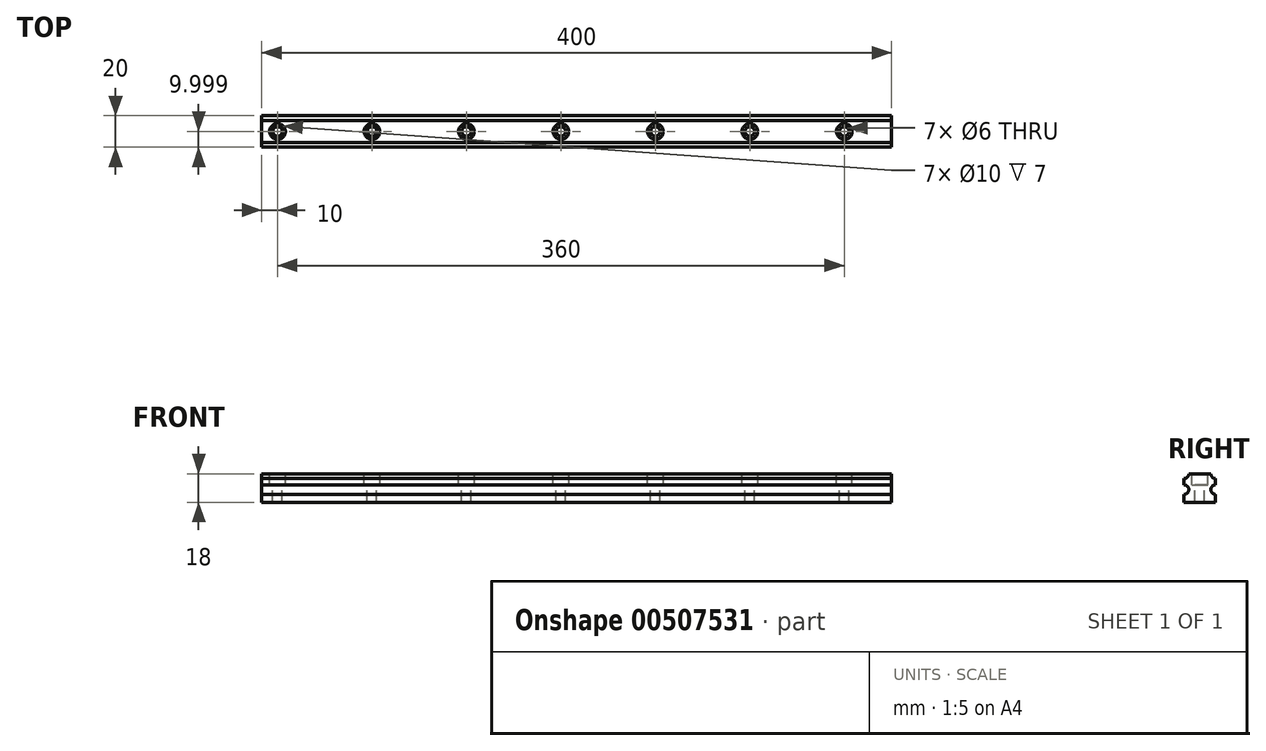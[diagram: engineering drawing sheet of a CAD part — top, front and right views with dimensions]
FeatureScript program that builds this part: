
annotation { "Feature Type Name" : "Feature", "Feature Type Description" : "" }
export const myFeature = defineFeature(function(context is Context, id is Id, definition is map)
    precondition{}
    {
        {
            var Q0;
            Q0=qCreatedBy(makeId("Right.planeOp"),FACE);
            var sketch = newSketch(context, id + "F0", { "sketchPlane" : qUnion([Q0])});
            skLineSegment(sketch, "E0", {"start": v(-26.04, 0) * mm, "end": v(-26.04, 5) * mm});
            skLineSegment(sketch, "E1", {"start": v(-26.04, 11) * mm, "end": v(-26.04, 15) * mm});
            skLineSegment(sketch, "E2", {"start": v(-23.04, 18) * mm, "end": v(-9.04, 18) * mm});
            skLineSegment(sketch, "E3", {"start": v(-6.04, 15) * mm, "end": v(-6.04, 11) * mm});
            skLineSegment(sketch, "E4", {"start": v(-6.04, 5) * mm, "end": v(-6.04, 0) * mm});
            skLineSegment(sketch, "E5", {"start": v(-6.04, 0) * mm, "end": v(-26.04, 0) * mm});
            skArc(sketch, "E6", {"start": v(-26.04, 5) * mm, "mid": v(-23.04, 8) * mm, "end": v(-26.04, 11) * mm});
            skArc(sketch, "E7", {"start": v(-6.04, 11) * mm, "mid": v(-9.04, 8) * mm, "end": v(-6.04, 5) * mm});
            skArc(sketch, "E8", {"start": v(-26.04, 15) * mm, "mid": v(-23.92, 15.88) * mm, "end": v(-23.04, 18) * mm});
            skArc(sketch, "E9", {"start": v(-9.04, 18) * mm, "mid": v(-8.16, 15.88) * mm, "end": v(-6.04, 15) * mm});
            skSolve(sketch);
        }
        {
            var Q0;
            Q0 = qSketchRegion(id + "F0", true);
            extrude(context, id + "F1", {"entities" : qUnion([Q0]), "offsetDistance" : 25 * mm, "depth" : 400 * mm});
        }
        {
            var Q0;
            Q0=makeQuery(id+"F1.opExtrude","SWEPT_FACE",FACE,{"disambiguationData":[OSD([sQuery(id+"F0.wireOp",EDGE,"E2")])]});
            var sketch = newSketch(context, id + "F2", { "sketchPlane" : qUnion([Q0])});
            skCircle(sketch, "E10", {"center": v(10, -16.04) * mm, "radius": 3 * mm});
            skCircle(sketch, "E11", {"center": v(70, -16.04) * mm, "radius": 3 * mm});
            skCircle(sketch, "E12", {"center": v(130, -16.04) * mm, "radius": 3 * mm});
            skCircle(sketch, "E13", {"center": v(190, -16.04) * mm, "radius": 3 * mm});
            skCircle(sketch, "E14", {"center": v(250, -16.04) * mm, "radius": 3 * mm});
            skCircle(sketch, "E15", {"center": v(310, -16.04) * mm, "radius": 3 * mm});
            skCircle(sketch, "E16", {"center": v(370, -16.04) * mm, "radius": 3 * mm});
            skCircle(sketch, "E17", {"center": v(430, -16.04) * mm, "radius": 3 * mm});
            skCircle(sketch, "E18", {"center": v(490, -16.04) * mm, "radius": 3 * mm});
            skCircle(sketch, "E19", {"center": v(550, -16.04) * mm, "radius": 3 * mm});
            skCircle(sketch, "E20", {"center": v(610, -16.04) * mm, "radius": 3 * mm});
            skCircle(sketch, "E21", {"center": v(670, -16.04) * mm, "radius": 3 * mm});
            skCircle(sketch, "E22", {"center": v(730, -16.04) * mm, "radius": 3 * mm});
            skCircle(sketch, "E23", {"center": v(790, -16.04) * mm, "radius": 3 * mm});
            skCircle(sketch, "E24", {"center": v(850, -16.04) * mm, "radius": 3 * mm});
            skCircle(sketch, "E25", {"center": v(910, -16.04) * mm, "radius": 3 * mm});
            skCircle(sketch, "E26", {"center": v(970, -16.04) * mm, "radius": 3 * mm});
            skCircle(sketch, "E27", {"center": v(1030, -16.04) * mm, "radius": 3 * mm});
            skCircle(sketch, "E28", {"center": v(1090, -16.04) * mm, "radius": 3 * mm});
            skCircle(sketch, "E29", {"center": v(1150, -16.04) * mm, "radius": 3 * mm});
            skCircle(sketch, "E30", {"center": v(1210, -16.04) * mm, "radius": 3 * mm});
            skCircle(sketch, "E31", {"center": v(1270, -16.04) * mm, "radius": 3 * mm});
            skCircle(sketch, "E32", {"center": v(1330, -16.04) * mm, "radius": 3 * mm});
            skCircle(sketch, "E33", {"center": v(1390, -16.04) * mm, "radius": 3 * mm});
            skCircle(sketch, "E34", {"center": v(1450, -16.04) * mm, "radius": 3 * mm});
            skCircle(sketch, "E35", {"center": v(1510, -16.04) * mm, "radius": 3 * mm});
            skCircle(sketch, "E36", {"center": v(1570, -16.04) * mm, "radius": 3 * mm});
            skCircle(sketch, "E37", {"center": v(1630, -16.04) * mm, "radius": 3 * mm});
            skCircle(sketch, "E38", {"center": v(1690, -16.04) * mm, "radius": 3 * mm});
            skCircle(sketch, "E39", {"center": v(1750, -16.04) * mm, "radius": 3 * mm});
            skCircle(sketch, "E40", {"center": v(1810, -16.04) * mm, "radius": 3 * mm});
            skCircle(sketch, "E41", {"center": v(1870, -16.04) * mm, "radius": 3 * mm});
            skCircle(sketch, "E42", {"center": v(1930, -16.04) * mm, "radius": 3 * mm});
            skCircle(sketch, "E43", {"center": v(1990, -16.04) * mm, "radius": 3 * mm});
            skSolve(sketch);
        }
        {
            var Q0;
            Q0 = qSketchRegion(id + "F2", true);
            extrude(context, id + "F3", {"entities" : qUnion([Q0]), "operationType" : NewBodyOperationType.REMOVE, "oppositeDirection" : true, "depth" : 18 * mm});
        }
        {
            var Q0;
            Q0=makeQuery(id+"F1.opExtrude","SWEPT_FACE",FACE,{"disambiguationData":[OSD([sQuery(id+"F0.wireOp",EDGE,"E2")])]});
            var sketch = newSketch(context, id + "F4", { "sketchPlane" : qUnion([Q0])});
            skCircle(sketch, "E44", {"center": v(10, -16.04) * mm, "radius": 5 * mm});
            skCircle(sketch, "E45", {"center": v(70, -16.04) * mm, "radius": 5 * mm});
            skCircle(sketch, "E46", {"center": v(130, -16.04) * mm, "radius": 5 * mm});
            skCircle(sketch, "E47", {"center": v(190, -16.04) * mm, "radius": 5 * mm});
            skCircle(sketch, "E48", {"center": v(250, -16.04) * mm, "radius": 5 * mm});
            skCircle(sketch, "E49", {"center": v(310, -16.04) * mm, "radius": 5 * mm});
            skCircle(sketch, "E50", {"center": v(370, -16.04) * mm, "radius": 5 * mm});
            skSolve(sketch);
        }
        {
            var Q0;
            Q0 = qSketchRegion(id + "F4", true);
            extrude(context, id + "F5", {"entities" : qUnion([Q0]), "operationType" : NewBodyOperationType.REMOVE, "oppositeDirection" : true, "depth" : 7 * mm});
        }
    });
